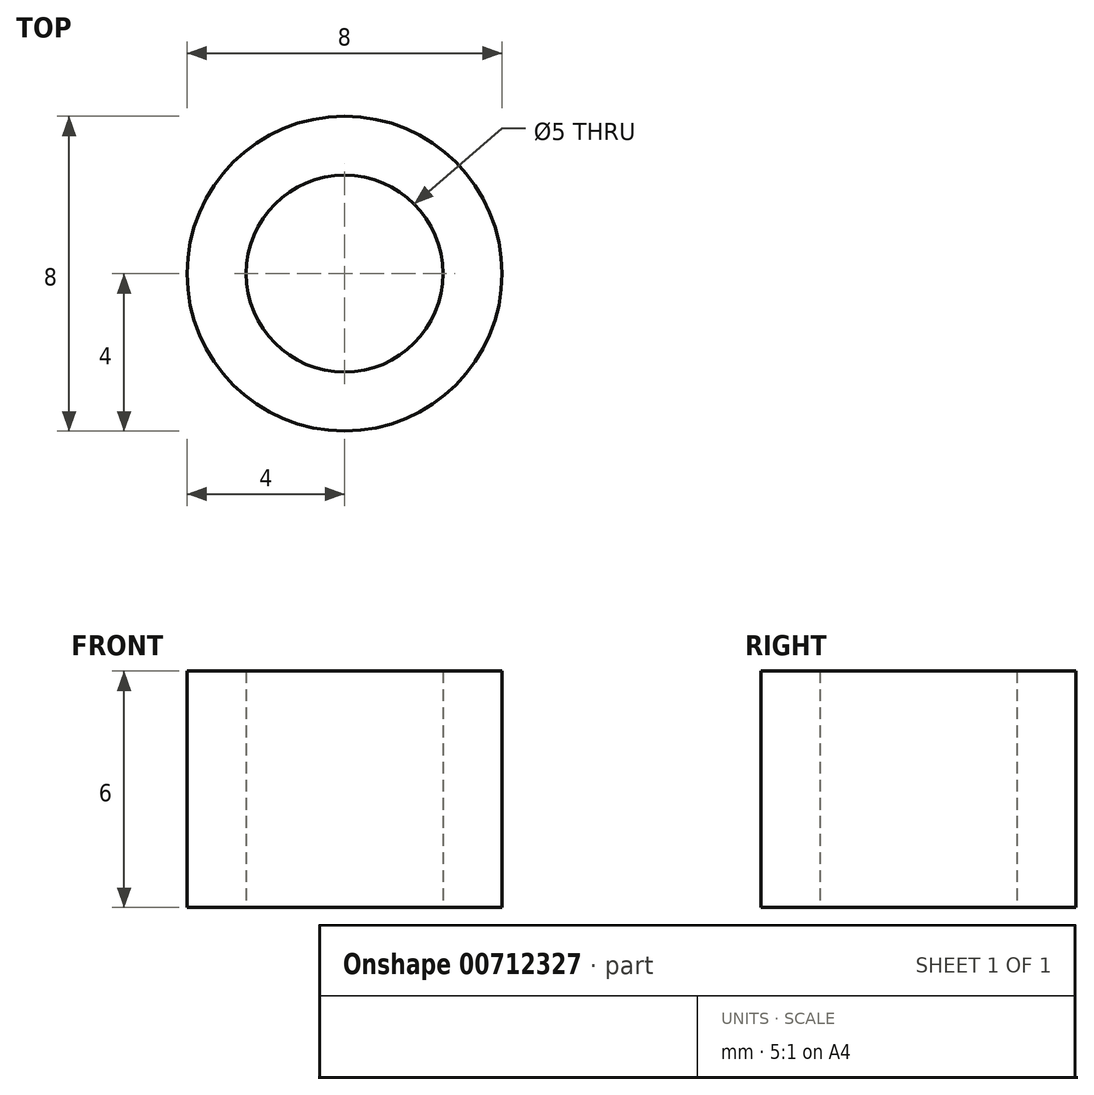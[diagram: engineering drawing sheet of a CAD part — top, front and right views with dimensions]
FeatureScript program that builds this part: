
annotation { "Feature Type Name" : "Feature", "Feature Type Description" : "" }
export const myFeature = defineFeature(function(context is Context, id is Id, definition is map)
    precondition{}
    {
        {
            var Q0;
            Q0=qCreatedBy(makeId("Top.planeOp"),FACE);
            var sketch = newSketch(context, id + "F0", { "sketchPlane" : qUnion([Q0])});
            skCircle(sketch, "E0", {"center": v(0, 0) * mm, "radius": 4 * mm});
            skCircle(sketch, "E1", {"center": v(0, 0) * mm, "radius": 2.5 * mm});
            skSolve(sketch);
        }
        {
            var Q0;
            Q0=makeQuery(id+"F0.imprint","IMPRINT",FACE,{"disambiguationData":[TD([[makeQuery(id+"F0.imprint","IMPRINT",EDGE,{"derivedFrom":sQuery(id+"F0.wireOp",EDGE,"E0")}),1.0]])]});
            extrude(context, id + "F1", {"entities" : qUnion([Q0]), "depth" : 6 * mm, "offsetDistance" : 25 * mm});
        }
    });
